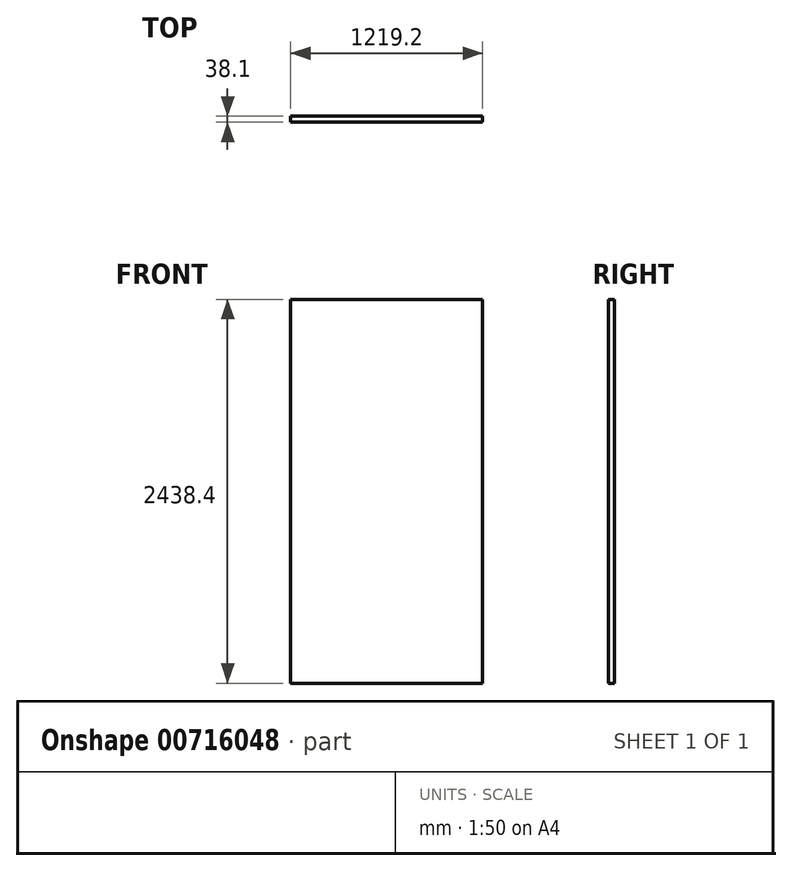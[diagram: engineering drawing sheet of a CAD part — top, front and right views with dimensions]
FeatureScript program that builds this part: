
annotation { "Feature Type Name" : "Feature", "Feature Type Description" : "" }
export const myFeature = defineFeature(function(context is Context, id is Id, definition is map)
    precondition{}
    {
        {
            var Q0;
            Q0=qCreatedBy(makeId("Front.planeOp"),FACE);
            var sketch = newSketch(context, id + "F0", { "sketchPlane" : qUnion([Q0])});
            skLineSegment(sketch, "E0.bottom", {"start": v(-609.6, 1219.2) * mm, "end": v(609.6, 1219.2) * mm});
            skLineSegment(sketch, "E0.top", {"start": v(-609.6, -1219.2) * mm, "end": v(609.6, -1219.2) * mm});
            skLineSegment(sketch, "E0.left", {"start": v(-609.6, 1219.2) * mm, "end": v(-609.6, -1219.2) * mm});
            skLineSegment(sketch, "E0.right", {"start": v(609.6, 1219.2) * mm, "end": v(609.6, -1219.2) * mm});
            skSolve(sketch);
        }
        {
            var Q0;
            Q0=makeQuery(id+"F0.imprint","IMPRINT",FACE,{"disambiguationData":[TD([[makeQuery(id+"F0.imprint","IMPRINT",EDGE,{"derivedFrom":sQuery(id+"F0.wireOp",EDGE,"E0.bottom")}),-1.0]])]});
            extrude(context, id + "F1", {"entities" : qUnion([Q0]), "depth" : 38.1 * mm, "offsetDistance" : 25.4 * mm});
        }
    });
